# Revit family: square-non-tapered-recessed-panel-column-bim
name_source: partatom
category: Columns
units: mm (PartAtom-declared; Revit-internal decimal feet)

## family parameters
Automatically joins geometry to walls = Yes
Classification Number = 23.25.30.11.14.11
Cut with Voids When Loaded = No
Shared = No
Show family pre-cut in plan views = Yes

## types (4) — shared parameters
Assembly Code = 066000
Description = Load-bearing or decorative composite column with Tuscan, Doric, or Attic cap/base, available in Cast Fiberglass, Lightweight Fiberglass, Synthetic Stone, or GFRC.
Manufacturer = Royal Corinthian
Material = RoyalStone Limestone
Model = Square Non-Tapered Recessed Panel Column
Product Line = RoyalCast / RoyaLite / RoyalStone / RoyalGFRC
URL = https://royalcorinthian.com

## per-type parameters (varying)
| type | Tuscan Base_Width | Tuscan Cap_Width | Width |
| Square Non-Tapered Recessed Panel Column 8" | 0' - 4 1/2" | 0' - 5 1/2" | 0' - 8" |
| Square Non-Tapered Recessed Panel Column 10" | 0' - 5 1/2" | 0' - 7" | 0' - 10" |
| Square Non-Tapered Recessed Panel Column 12" | 0' - 7" | 0' - 8 1/2" | 1' - 0" |
| Square Non-Tapered Recessed Panel Column 14" | 0' - 8" | 0' - 10" | 1' - 2" |

## geometry (parser evidence)
native form markers: Sweep x15
no freeform markers — native parametric forms only
